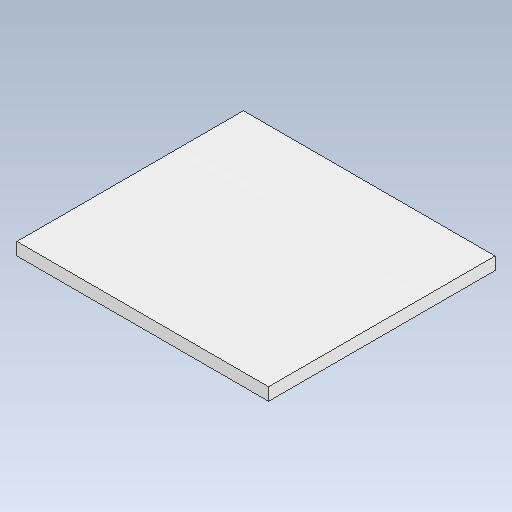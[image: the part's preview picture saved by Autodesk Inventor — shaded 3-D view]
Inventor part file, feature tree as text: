
AUTODESK INVENTOR PART (.ipt)
format: ipt  version: 2021 (Build 250183000, 183)  size: 90,112 bytes
history: native  units: mm
features: extrude x1, sketch x1
ambient origin geometry x8: Origin, YZ Plane, XZ Plane, XY Plane, X Axis, Y Axis, Z Axis, Center Point
bodies: Solid1 (feature_tree)
feature tree (2):
  extrude  "Extrusion1"  Depth=90.0mm
  sketch  "Sketch1"  dims[d0=100.0mm d1=90.0mm d2=5.0mm d3=0.0mm]
